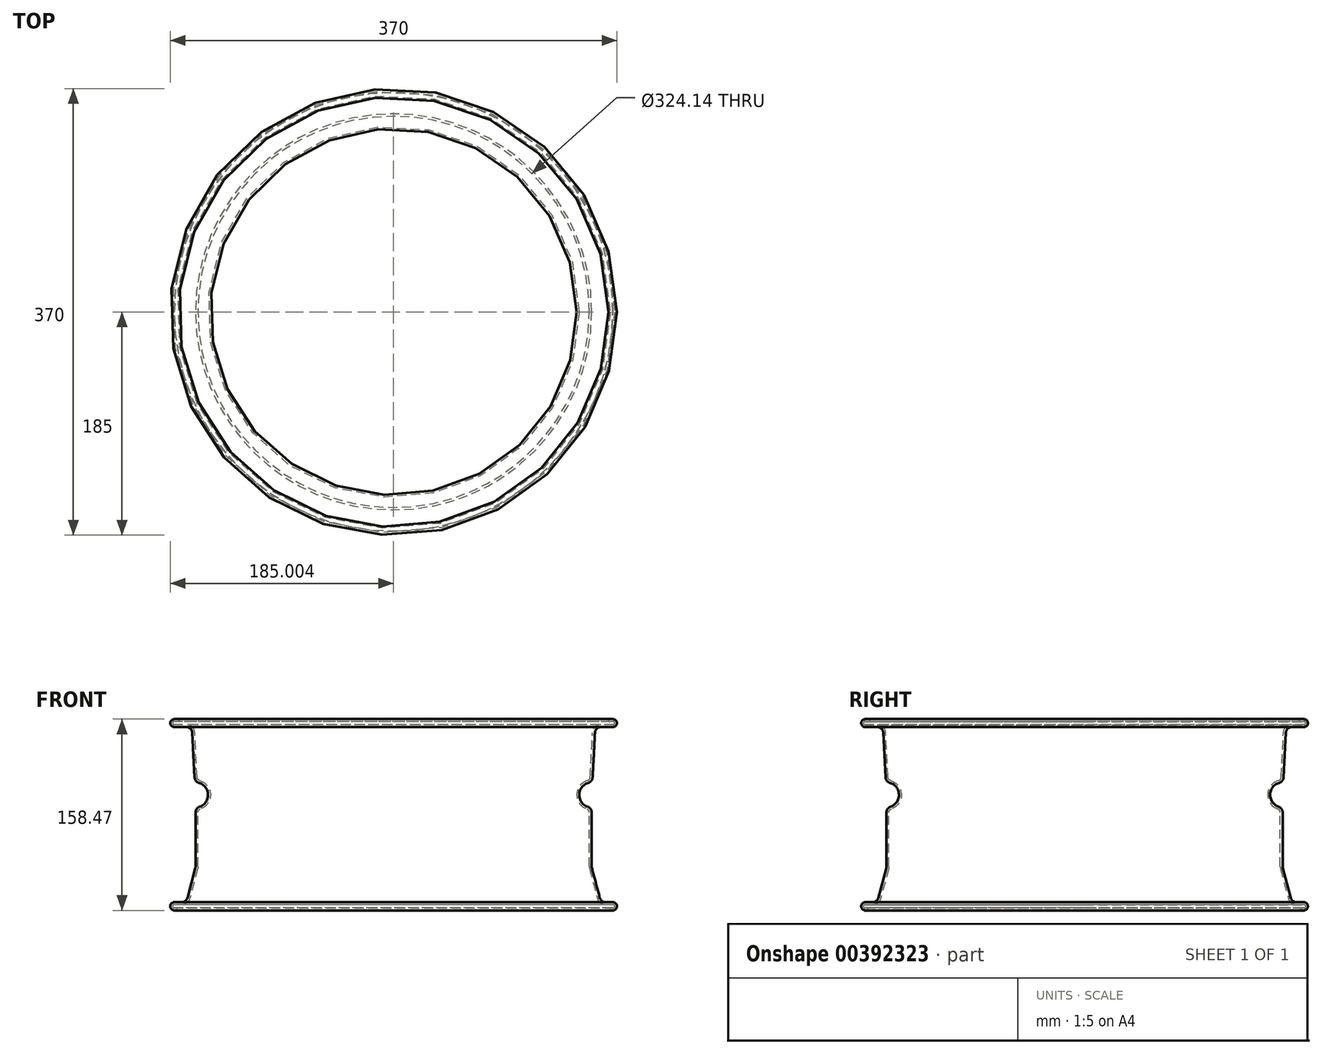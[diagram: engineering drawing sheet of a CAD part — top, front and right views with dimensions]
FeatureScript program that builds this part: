
annotation { "Feature Type Name" : "Feature", "Feature Type Description" : "" }
export const myFeature = defineFeature(function(context is Context, id is Id, definition is map)
    precondition{}
    {
        {
            var Q0;
            Q0=qCreatedBy(makeId("Front.planeOp"),FACE);
            var sketch = newSketch(context, id + "F0", { "sketchPlane" : qUnion([Q0])});
            skLineSegment(sketch, "E0", {"start": v(-126.12, -19.06) * mm, "end": v(-119.96, -19.06) * mm});
            skLineSegment(sketch, "E1", {"start": v(-115.13, -15.34) * mm, "end": v(-108.6, 9.32) * mm});
            skLineSegment(sketch, "E2", {"start": v(-108.44, 10.6) * mm, "end": v(-108.44, 55.33) * mm});
            skLineSegment(sketch, "E3", {"start": v(-109.2, 84.4) * mm, "end": v(-111.12, 121.39) * mm});
            skLineSegment(sketch, "E4", {"start": v(-126.12, 132.63) * mm, "end": v(-123.42, 132.63) * mm});
            skLineSegment(sketch, "E5", {"start": v(-125.97, -25.84) * mm, "end": v(-124.85, -25.84) * mm});
            skArc(sketch, "E6", {"start": v(-125.97, -25.84) * mm, "mid": v(-129.37, -22.52) * mm, "end": v(-126.12, -19.06) * mm});
            skLineSegment(sketch, "E7", {"start": v(-126.12, 126.13) * mm, "end": v(-116.12, 126.13) * mm});
            skArc(sketch, "E8", {"start": v(-126.12, 126.13) * mm, "mid": v(-129.37, 129.38) * mm, "end": v(-126.12, 132.63) * mm});
            skArc(sketch, "E9", {"start": v(-105.58, 79.86) * mm, "mid": v(-98.06, 70.15) * mm, "end": v(-105.06, 60.06) * mm});
            skPoint(sketch, "E10.visualSharp", {"position": v(-111.37, 126.13) * mm});
            skArc(sketch, "E10.filletArc", {"start": v(-111.12, 121.39) * mm, "mid": v(-112.67, 124.76) * mm, "end": v(-116.12, 126.13) * mm});
            skArc(sketch, "E11.filletArc", {"start": v(-109.2, 84.4) * mm, "mid": v(-108.11, 81.55) * mm, "end": v(-105.58, 79.86) * mm});
            skPoint(sketch, "E12.visualSharp", {"position": v(-108.44, 59.5) * mm});
            skArc(sketch, "E12.filletArc", {"start": v(-105.06, 60.06) * mm, "mid": v(-107.5, 58.24) * mm, "end": v(-108.44, 55.33) * mm});
            skPoint(sketch, "E13.visualSharp", {"position": v(-108.44, 9.94) * mm});
            skArc(sketch, "E13.filletArc", {"start": v(-108.6, 9.32) * mm, "mid": v(-108.48, 9.95) * mm, "end": v(-108.44, 10.6) * mm});
            skPoint(sketch, "E14.visualSharp", {"position": v(-116.12, -19.06) * mm});
            skArc(sketch, "E14.filletArc", {"start": v(-119.96, -19.06) * mm, "mid": v(-116.91, -18.02) * mm, "end": v(-115.13, -15.34) * mm});
            skLineSegment(sketch, "E15.0", {"start": v(55.63, 137.95) * mm, "end": v(55.63, -34.23) * mm});
            skLineSegment(sketch, "E16.0", {"start": v(215.63, 137.95) * mm, "end": v(215.63, -34.23) * mm, "construction": true});
            skLineSegment(sketch, "E17.0", {"start": v(-126.29, 128.13) * mm, "end": v(-116.12, 128.13) * mm});
            skArc(sketch, "E18.0", {"start": v(-109.13, 121.49) * mm, "mid": v(-111.3, 126.2) * mm, "end": v(-116.12, 128.13) * mm});
            skLineSegment(sketch, "E19.0", {"start": v(-126.12, 130.63) * mm, "end": v(-123.42, 130.63) * mm});
            skArc(sketch, "E20", {"start": v(-126.29, 128.13) * mm, "mid": v(-127.54, 129.47) * mm, "end": v(-126.12, 130.63) * mm});
            skArc(sketch, "E21", {"start": v(-123.42, 132.63) * mm, "mid": v(-122.42, 131.63) * mm, "end": v(-123.42, 130.63) * mm});
            skLineSegment(sketch, "E22.0", {"start": v(-107.2, 84.5) * mm, "end": v(-109.13, 121.5) * mm});
            skArc(sketch, "E23.0", {"start": v(-105.03, 81.78) * mm, "mid": v(-97.6, 75.87) * mm, "end": v(-96.54, 66.44) * mm});
            skArc(sketch, "E24", {"start": v(-105.03, 81.78) * mm, "mid": v(-106.55, 82.8) * mm, "end": v(-107.2, 84.5) * mm});
            skLineSegment(sketch, "E25.0", {"start": v(-106.44, 10.6) * mm, "end": v(-106.44, 55.33) * mm});
            skLineSegment(sketch, "E26.0", {"start": v(-125.97, -23.84) * mm, "end": v(-124.85, -23.84) * mm});
            skLineSegment(sketch, "E27.0", {"start": v(-126.12, -21.06) * mm, "end": v(-119.96, -21.06) * mm});
            skArc(sketch, "E28.0", {"start": v(-119.96, -21.06) * mm, "mid": v(-115.7, -19.6) * mm, "end": v(-113.2, -15.85) * mm});
            skLineSegment(sketch, "E29.0", {"start": v(-113.2, -15.85) * mm, "end": v(-106.67, 8.8) * mm});
            skArc(sketch, "E30", {"start": v(-126.12, -21.06) * mm, "mid": v(-127.51, -22.52) * mm, "end": v(-125.97, -23.84) * mm});
            skArc(sketch, "E31", {"start": v(-124.85, -25.84) * mm, "mid": v(-123.85, -24.84) * mm, "end": v(-124.85, -23.84) * mm});
            skArc(sketch, "E32", {"start": v(-106.44, 10.6) * mm, "mid": v(-106.5, 9.7) * mm, "end": v(-106.67, 8.8) * mm});
            skArc(sketch, "E33", {"start": v(-104.41, 58.17) * mm, "mid": v(-105.88, 57.08) * mm, "end": v(-106.44, 55.33) * mm});
            skArc(sketch, "E34", {"start": v(-96.54, 66.44) * mm, "mid": v(-99.47, 61.34) * mm, "end": v(-104.41, 58.17) * mm});
            skLineSegment(sketch, "E35", {"start": v(-129.37, -22.8) * mm, "end": v(-129.37, 131.96) * mm, "construction": true});
            skSolve(sketch);
        }
        {
            var Q0;
            Q0=makeQuery(id+"F0.imprint","IMPRINT",FACE,{"disambiguationData":[TD([[makeQuery(id+"F0.imprint","IMPRINT",EDGE,{"derivedFrom":sQuery(id+"F0.wireOp",EDGE,"E0")}),-1.0]])]});
            var Q1;
            Q1=sQuery(id+"F0.wireOp",EDGE,"E29.0");
            var Q2;
            Q2=sQuery(id+"F0.wireOp",EDGE,"E1");
            var Q3;
            Q3=sQuery(id+"F0.wireOp",EDGE,"E23.0");
            var Q4;
            Q4=sQuery(id+"F0.wireOp",EDGE,"E3");
            var Q5;
            Q5=sQuery(id+"F0.wireOp",EDGE,"E2");
            var Q6;
            Q6=sQuery(id+"F0.wireOp",EDGE,"9226ba75-6c61-455b-819a-41e9fab7ad21.0");
            var Q7;
            Q7=sQuery(id+"F0.wireOp",EDGE,"ZDSL2yBL-a5dj-NfuI-e1ZX-pN1Fczb499Jl");
            var Q8;
            Q8=sQuery(id+"F0.wireOp",EDGE,"E9");
            var Q9;
            Q9=sQuery(id+"F0.wireOp",EDGE,"E22.0");
            var Q10;
            Q10=sQuery(id+"F0.wireOp",EDGE,"E25.0");
            var Q11;
            Q11=sQuery(id+"F0.wireOp",EDGE,"E18.0");
            var Q12;
            Q12=sQuery(id+"F0.wireOp",EDGE,"E12.filletArc");
            var Q13;
            Q13=sQuery(id+"F0.wireOp",EDGE,"E11.filletArc");
            var Q14;
            Q14=sQuery(id+"F0.wireOp",EDGE,"E33");
            var Q15;
            Q15=sQuery(id+"F0.wireOp",EDGE,"E34");
            var Q16;
            Q16=sQuery(id+"F0.wireOp",EDGE,"E10.filletArc");
            var Q17;
            Q17=sQuery(id+"F0.wireOp",EDGE,"E17.0");
            var Q18;
            Q18=sQuery(id+"F0.wireOp",EDGE,"E27.0");
            var Q19;
            Q19=sQuery(id+"F0.wireOp",EDGE,"E0");
            var Q20;
            Q20=sQuery(id+"F0.wireOp",EDGE,"6acfbd19-7370-434e-ac6c-36c463c4ff00");
            var Q21;
            Q21=sQuery(id+"F0.wireOp",EDGE,"E6");
            var Q22;
            Q22=sQuery(id+"F0.wireOp",EDGE,"E7");
            var Q23;
            Q23=sQuery(id+"F0.wireOp",EDGE,"E28.0");
            var Q24;
            Q24=sQuery(id+"F0.wireOp",EDGE,"E14.filletArc");
            var Q25;
            Q25=sQuery(id+"F0.wireOp",EDGE,"E24");
            var Q26;
            Q26=sQuery(id+"F0.wireOp",EDGE,"f06582b2-a28b-43a5-8e16-6c8bdb3ea228.filletArc");
            var Q27;
            Q27=sQuery(id+"F0.wireOp",EDGE,"c2f34cc3-9568-4277-b26f-fe3e7d1ce806.filletArc");
            var Q28;
            Q28=sQuery(id+"F0.wireOp",EDGE,"E20");
            var Q29;
            Q29=sQuery(id+"F0.wireOp",EDGE,"E32");
            var Q30;
            Q30=sQuery(id+"F0.wireOp",EDGE,"E8");
            var Q31;
            Q31=sQuery(id+"F0.wireOp",EDGE,"E21");
            var Q32;
            Q32=sQuery(id+"F0.wireOp",EDGE,"E19.0");
            var Q33;
            Q33=sQuery(id+"F0.wireOp",EDGE,"E13.filletArc");
            var Q34;
            Q34=sQuery(id+"F0.wireOp",EDGE,"E4");
            var Q35;
            Q35=sQuery(id+"F0.wireOp",EDGE,"E31");
            var Q36;
            Q36=sQuery(id+"F0.wireOp",EDGE,"E5");
            var Q37;
            Q37=sQuery(id+"F0.wireOp",EDGE,"E30");
            var Q38;
            Q38=sQuery(id+"F0.wireOp",EDGE,"E26.0");
            var Q39;
            Q39=sQuery(id+"F0.wireOp",EDGE,"E15.0");
            revolve(context, id + "F1", {"entities" : qUnion([Q0]), "surfaceEntities" : qUnion([Q1, Q2, Q3, Q4, Q5, Q6, Q7, Q8, Q9, Q10, Q11, Q12, Q13, Q14, Q15, Q16, Q17, Q18, Q19, Q20, Q21, Q22, Q23, Q24, Q25, Q26, Q27, Q28, Q29, Q30, Q31, Q32, Q33, Q34, Q35, Q36, Q37, Q38]), "axis" : qUnion([Q39]), "revolveType" : RevolveType.FULL});
        }
    });
